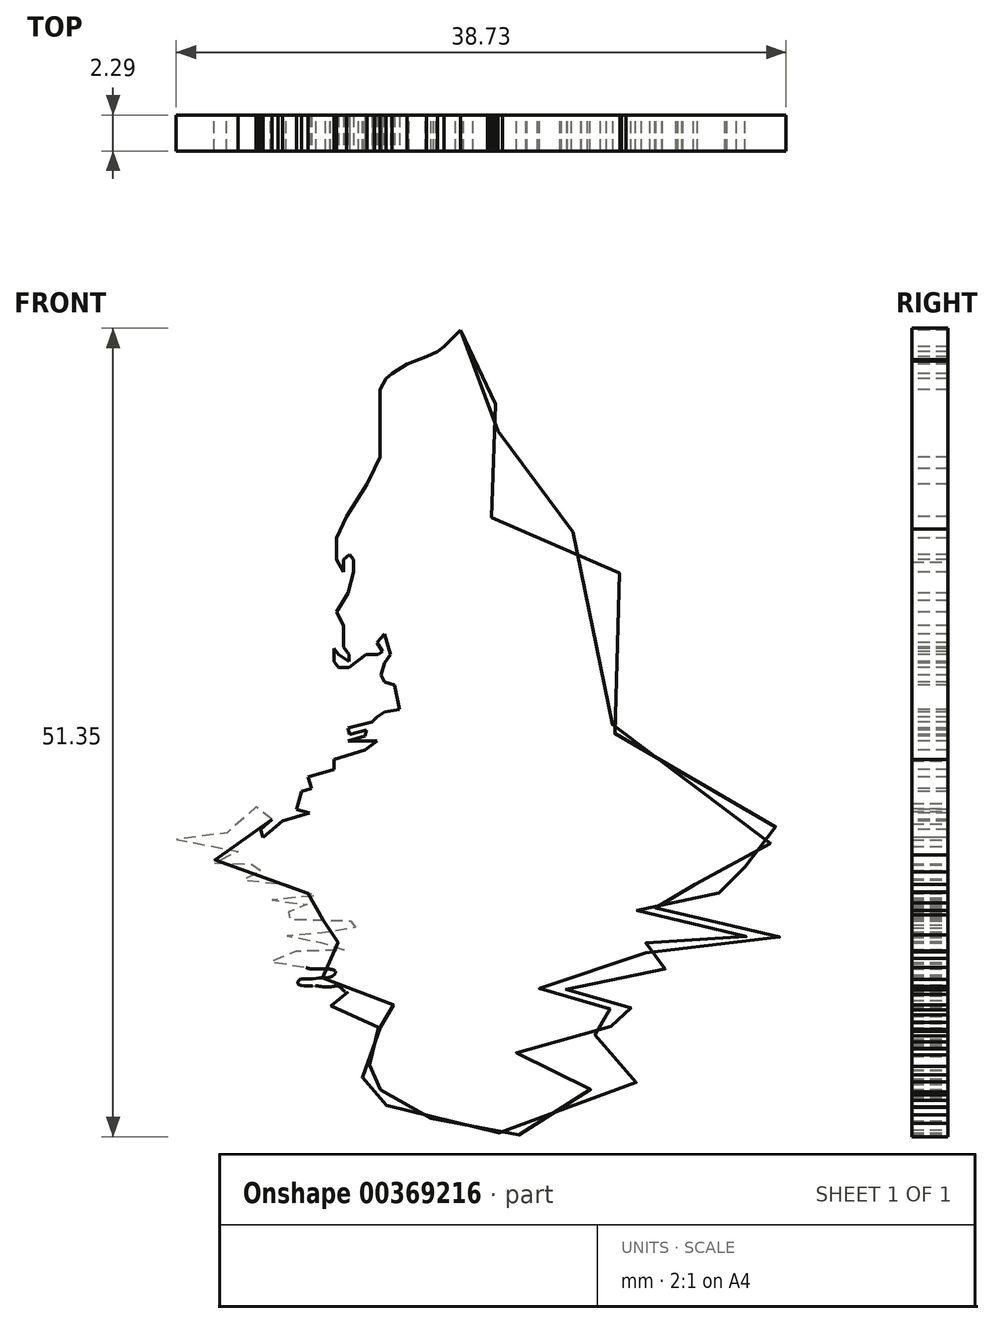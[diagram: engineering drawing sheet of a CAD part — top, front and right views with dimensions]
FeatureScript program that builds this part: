
annotation { "Feature Type Name" : "Feature", "Feature Type Description" : "" }
export const myFeature = defineFeature(function(context is Context, id is Id, definition is map)
    precondition{}
    {
        {
            var Q0;
            Q0=qCreatedBy(makeId("Front.planeOp"),FACE);
            var sketch = newSketch(context, id + "F0", { "sketchPlane" : qUnion([Q0])});
            skLineSegment(sketch, "E0", {"start": v(-10.1, 17.9) * mm, "end": v(-11.16, 16.85) * mm});
            skLineSegment(sketch, "E1", {"start": v(-11.16, 16.85) * mm, "end": v(-11.55, 16.52) * mm});
            skLineSegment(sketch, "E2", {"start": v(-11.55, 16.52) * mm, "end": v(-12.25, 16.22) * mm});
            skLineSegment(sketch, "E3", {"start": v(-12.25, 16.22) * mm, "end": v(-13.51, 15.72) * mm});
            skLineSegment(sketch, "E4", {"start": v(-13.51, 15.72) * mm, "end": v(-14.44, 15.12) * mm});
            skLineSegment(sketch, "E5", {"start": v(-14.44, 15.12) * mm, "end": v(-14.84, 14.82) * mm});
            skLineSegment(sketch, "E6", {"start": v(-14.84, 14.82) * mm, "end": v(-15.2, 14.13) * mm});
            skLineSegment(sketch, "E7", {"start": v(-15.2, 14.13) * mm, "end": v(-15.2, 12.83) * mm});
            skLineSegment(sketch, "E8", {"start": v(-15.2, 12.83) * mm, "end": v(-15.2, 11.57) * mm});
            skLineSegment(sketch, "E9", {"start": v(-15.2, 11.57) * mm, "end": v(-15.2, 10.54) * mm});
            skLineSegment(sketch, "E10", {"start": v(-15.2, 10.54) * mm, "end": v(-15.2, 9.81) * mm});
            skLineSegment(sketch, "E11", {"start": v(-15.2, 9.81) * mm, "end": v(-15.57, 9.08) * mm});
            skLineSegment(sketch, "E12", {"start": v(-15.57, 9.08) * mm, "end": v(-16.03, 8.12) * mm});
            skLineSegment(sketch, "E13", {"start": v(-16.03, 8.12) * mm, "end": v(-17.36, 6.04) * mm});
            skLineSegment(sketch, "E14", {"start": v(-17.36, 6.04) * mm, "end": v(-17.97, 4.7) * mm});
            skLineSegment(sketch, "E15", {"start": v(-17.97, 4.7) * mm, "end": v(-17.97, 3.31) * mm});
            skLineSegment(sketch, "E16", {"start": v(-17.97, 3.31) * mm, "end": v(-17.54, 2.52) * mm});
            skLineSegment(sketch, "E17", {"start": v(-17.54, 2.52) * mm, "end": v(-17.54, 3.31) * mm});
            skLineSegment(sketch, "E18", {"start": v(-17.54, 3.31) * mm, "end": v(-17.14, 3.63) * mm});
            skLineSegment(sketch, "E19", {"start": v(-17.14, 3.63) * mm, "end": v(-16.9, 3.31) * mm});
            skLineSegment(sketch, "E20", {"start": v(-16.9, 3.31) * mm, "end": v(-16.9, 2.52) * mm});
            skLineSegment(sketch, "E21", {"start": v(-16.9, 2.52) * mm, "end": v(-17.26, 1.18) * mm});
            skLineSegment(sketch, "E22", {"start": v(-17.26, 1.18) * mm, "end": v(-17.54, 0.7) * mm});
            skLineSegment(sketch, "E23", {"start": v(-17.54, 0.7) * mm, "end": v(-17.97, 0) * mm});
            skLineSegment(sketch, "E24", {"start": v(-17.97, 0) * mm, "end": v(-17.54, -0.87) * mm});
            skLineSegment(sketch, "E25", {"start": v(-17.54, -0.87) * mm, "end": v(-17.54, -1.42) * mm});
            skLineSegment(sketch, "E26", {"start": v(-17.54, -1.42) * mm, "end": v(-17.54, -2.25) * mm});
            skLineSegment(sketch, "E27", {"start": v(-17.54, -2.25) * mm, "end": v(-17.18, -2.73) * mm});
            skLineSegment(sketch, "E28", {"start": v(-17.18, -2.73) * mm, "end": v(-17.18, -3.16) * mm});
            skLineSegment(sketch, "E29", {"start": v(-17.18, -3.16) * mm, "end": v(-17.85, -2.73) * mm});
            skLineSegment(sketch, "E30", {"start": v(-17.85, -2.73) * mm, "end": v(-18.14, -2.34) * mm});
            skLineSegment(sketch, "E31", {"start": v(-18.14, -2.34) * mm, "end": v(-18.14, -3.16) * mm});
            skLineSegment(sketch, "E32", {"start": v(-18.14, -3.16) * mm, "end": v(-17.85, -3.54) * mm});
            skLineSegment(sketch, "E33", {"start": v(-17.85, -3.54) * mm, "end": v(-17.18, -3.54) * mm});
            skLineSegment(sketch, "E34", {"start": v(-17.18, -3.54) * mm, "end": v(-16.67, -3.16) * mm});
            skLineSegment(sketch, "E35", {"start": v(-16.67, -3.16) * mm, "end": v(-16.1, -2.73) * mm});
            skLineSegment(sketch, "E36", {"start": v(-16.1, -2.73) * mm, "end": v(-15.33, -2.73) * mm});
            skLineSegment(sketch, "E37", {"start": v(-15.33, -2.73) * mm, "end": v(-15.05, -2.51) * mm});
            skLineSegment(sketch, "E38", {"start": v(-15.05, -2.51) * mm, "end": v(-15.71, -2.51) * mm});
            skPoint(sketch, "E38.endSnap0", {"position": v(-15.71, -2.73) * mm});
            skLineSegment(sketch, "E39", {"start": v(-14.94, -1.42) * mm, "end": v(-15.4, -1.94) * mm});
            skLineSegment(sketch, "E40", {"start": v(-15.4, -1.94) * mm, "end": v(-15.05, -2.51) * mm});
            skLineSegment(sketch, "E41", {"start": v(-14.94, -1.42) * mm, "end": v(-14.54, -2.73) * mm});
            skLineSegment(sketch, "E42", {"start": v(-14.54, -2.73) * mm, "end": v(-14.94, -3.24) * mm});
            skLineSegment(sketch, "E43", {"start": v(-14.94, -3.24) * mm, "end": v(-15.15, -4) * mm});
            skLineSegment(sketch, "E44", {"start": v(-15.15, -4) * mm, "end": v(-14.94, -4.46) * mm});
            skLineSegment(sketch, "E45", {"start": v(-14.94, -4.46) * mm, "end": v(-14.29, -4.64) * mm});
            skLineSegment(sketch, "E46", {"start": v(-14.29, -4.64) * mm, "end": v(-13.99, -6.2) * mm});
            skLineSegment(sketch, "E47", {"start": v(-13.99, -6.2) * mm, "end": v(-14.94, -6.38) * mm});
            skLineSegment(sketch, "E48", {"start": v(-14.94, -6.38) * mm, "end": v(-15.4, -6.67) * mm});
            skLineSegment(sketch, "E49", {"start": v(-15.4, -6.67) * mm, "end": v(-15.71, -6.99) * mm});
            skLineSegment(sketch, "E50", {"start": v(-15.71, -6.99) * mm, "end": v(-17.26, -7.38) * mm});
            skLineSegment(sketch, "E51", {"start": v(-17.26, -7.38) * mm, "end": v(-17.16, -7.79) * mm});
            skLineSegment(sketch, "E52", {"start": v(-17.16, -7.79) * mm, "end": v(-16.07, -7.51) * mm});
            skLineSegment(sketch, "E53", {"start": v(-16.07, -7.51) * mm, "end": v(-16.17, -7.9) * mm});
            skLineSegment(sketch, "E54", {"start": v(-16.17, -7.9) * mm, "end": v(-17.26, -8.2) * mm});
            skLineSegment(sketch, "E55", {"start": v(-17.26, -8.2) * mm, "end": v(-15.4, -8.2) * mm});
            skLineSegment(sketch, "E56", {"start": v(-15.4, -8.2) * mm, "end": v(-16.17, -8.8) * mm});
            skLineSegment(sketch, "E57", {"start": v(-16.17, -8.8) * mm, "end": v(-17.26, -9.11) * mm});
            skLineSegment(sketch, "E58", {"start": v(-17.26, -9.11) * mm, "end": v(-18.14, -9.37) * mm});
            skLineSegment(sketch, "E59", {"start": v(-18.14, -9.37) * mm, "end": v(-18.14, -10.01) * mm});
            skLineSegment(sketch, "E60", {"start": v(-18.14, -10.01) * mm, "end": v(-19.06, -10.28) * mm});
            skLineSegment(sketch, "E61", {"start": v(-19.06, -10.28) * mm, "end": v(-19.77, -10.49) * mm});
            skLineSegment(sketch, "E62", {"start": v(-19.77, -10.49) * mm, "end": v(-19.56, -11.23) * mm});
            skLineSegment(sketch, "E63", {"start": v(-19.56, -11.23) * mm, "end": v(-20.2, -11.42) * mm});
            skLineSegment(sketch, "E64", {"start": v(-20.2, -11.42) * mm, "end": v(-20.51, -12.56) * mm});
            skLineSegment(sketch, "E65", {"start": v(-20.51, -12.56) * mm, "end": v(-19.68, -12.79) * mm});
            skLineSegment(sketch, "E66", {"start": v(-19.68, -12.79) * mm, "end": v(-21.41, -13.3) * mm});
            skLineSegment(sketch, "E67", {"start": v(-21.41, -13.3) * mm, "end": v(-22.65, -14.33) * mm});
            skLineSegment(sketch, "E68", {"start": v(-22.65, -14.33) * mm, "end": v(-22.8, -13.81) * mm});
            skPoint(sketch, "E68.endSnap0", {"position": v(-22.03, -13.81) * mm});
            skLineSegment(sketch, "E69", {"start": v(-22.8, -13.81) * mm, "end": v(-22.06, -13.2) * mm});
            skFitSpline(sketch, "E70", {"points": [v(-22.06, -13.2) * mm, v(-21.7, -12.85) * mm, v(-22.06, -12.4) * mm, v(-23.07, -12.24) * mm, v(-23.04, -12.66) * mm, v(-24.19, -12.52) * mm, v(-24.94, -14.1) * mm, v(-25.14, -14.47) * mm, v(-28.12, -14.33) * mm, v(-27.29, -14.83) * mm, v(-24.3, -15.03) * mm, v(-24.33, -15.4) * mm, v(-25.03, -15.47) * mm, v(-25.53, -15.59) * mm, v(-25.72, -15.8) * mm, v(-25.7, -16) * mm, v(-24.7, -16.06) * mm, v(-23.94, -16.09) * mm, v(-23.27, -16.03) * mm, v(-22.4, -16.12) * mm, v(-21.68, -16.48) * mm, v(-24.42, -16.5) * mm, v(-24.95, -16.93) * mm, v(-23.92, -17.03) * mm, v(-22.63, -17) * mm, v(-21.41, -17.06) * mm, v(-21.1, -17.42) * mm, v(-20.64, -17.79) * mm, v(-19.77, -17.89) * mm, v(-19.28, -17.99) * mm, v(-19.94, -18.19) * mm, v(-21.13, -18.32) * mm, v(-22.06, -18.32) * mm, v(-22.06, -18.59) * mm, v(-21, -18.62) * mm, v(-20.17, -18.62) * mm, v(-19.28, -18.55) * mm, v(-20.1, -18.85) * mm, v(-20.5, -19.08) * mm, v(-22.43, -19.08) * mm, v(-22.56, -19.38) * mm, v(-20.57, -19.51) * mm, v(-18.58, -19.58) * mm, v(-16.82, -19.61) * mm, v(-16.16, -19.58) * mm, v(-16.03, -19.81) * mm, v(-16.3, -20.05) * mm, v(-17.25, -19.98) * mm, v(-18.38, -20.01) * mm, v(-18.38, -20.38) * mm, v(-19.18, -20.38) * mm, v(-20.14, -20.34) * mm, v(-20.8, -20.34) * mm, v(-21.1, -20.54) * mm, v(-21.17, -20.84) * mm, v(-20.3, -20.94) * mm, v(-19.38, -20.97) * mm, v(-18.18, -21) * mm, v(-17.32, -21.04) * mm, v(-17.12, -21.3) * mm, v(-18.35, -21.57) * mm, v(-19.58, -21.54) * mm, v(-20.5, -21.57) * mm, v(-21.41, -21.57) * mm, v(-21.41, -21.94) * mm, v(-22.06, -21.97) * mm, v(-22.06, -22.4) * mm, v(-20.97, -22.47) * mm, v(-20.17, -22.4) * mm, v(-19.8, -22.63) * mm, v(-18.38, -22.7) * mm, v(-18.02, -22.9) * mm, v(-18.45, -23.23) * mm, v(-18.98, -23.26) * mm, v(-19.77, -23.33) * mm, v(-20.24, -23.33) * mm, v(-20.44, -23.6) * mm, v(-19.9, -23.76) * mm, v(-19.3, -23.76) * mm, v(-18.48, -23.83) * mm, v(-17.82, -23.8) * mm, v(-17.49, -24.1) * mm, v(-16.52, -24.13) * mm, v(-15, -24.16) * mm, v(-13.87, -24.2) * mm, v(-12.94, -24.36) * mm, v(-12.3, -24.62) * mm, v(-13.2, -24.92) * mm, v(-14.7, -24.96) * mm, v(-16.5, -25.02) * mm, v(-17.68, -25.02) * mm, v(-18.48, -25.05) * mm, v(-18.81, -25.22) * mm, v(-21.1, -25.22) * mm, v(-21.17, -25.39) * mm, v(-21, -25.52) * mm, v(-20.37, -25.59) * mm, v(-19.08, -25.69) * mm, v(-17.88, -25.69) * mm, v(-17.29, -25.69) * mm, v(-16.66, -25.98) * mm, v(-15.13, -26.05) * mm, v(-15.06, -26.25) * mm, v(-15.4, -26.42) * mm, v(-16, -26.48) * mm, v(-16.2, -26.81) * mm, v(-15.76, -26.95) * mm, v(-15.16, -27.08) * mm, v(-15.4, -27.48) * mm, v(-18.55, -27.54) * mm, v(-18.51, -28.17) * mm, v(-17.92, -28.1) * mm, v(-17.05, -28.24) * mm, v(-16.32, -28.2) * mm, v(-16.3, -28.7) * mm, v(-15.74, -28.81) * mm, v(-15.74, -29.12) * mm, v(-16.42, -29.1) * mm, v(-16.56, -29.33) * mm, v(-16.25, -29.54) * mm, v(-17.26, -29.63) * mm, v(-18.32, -29.68) * mm, v(-18.65, -29.73) * mm, v(-18.62, -30) * mm, v(-18.3, -29.96) * mm, v(-17.78, -29.96) * mm, v(-17.52, -30.27) * mm, v(-16.04, -30.34) * mm, v(-15.4, -30.34) * mm, v(-14.54, -30.38) * mm, v(-13.72, -30.38) * mm, v(-13.41, -30.57) * mm, v(-13.44, -30.83) * mm, v(-13.95, -30.83) * mm, v(-14.54, -30.92) * mm, v(-15.1, -30.95) * mm, v(-15.24, -31.13) * mm, v(-14.75, -31.37) * mm, v(-13.93, -31.4) * mm, v(-12.95, -31.49) * mm, v(-11.66, -31.84) * mm, v(-11.87, -32.05) * mm, v(-11.98, -32.24) * mm, v(-11.5, -32.33) * mm, v(-10.44, -32.45) * mm, v(-10.58, -32.75) * mm, v(-11.05, -32.9) * mm, v(-11.47, -32.92) * mm, v(-11.77, -32.94) * mm, v(-11.77, -33.17) * mm, v(-11.2, -33.17) * mm, v(-10.58, -33.15) * mm, v(-9.52, -33.15) * mm, v(-8.49, -33.15) * mm, v(-7.13, -33.13) * mm, v(-4.83, -33.2) * mm, v(-4.66, -32.54) * mm, v(-3.75, -32.44) * mm, v(-3.52, -31.93) * mm, v(-1.98, -31.9) * mm, v(-1.98, -31.46) * mm, v(-2.45, -31.46) * mm, v(-2.45, -31.06) * mm, v(-3.2, -31.02) * mm, v(-3.24, -30.67) * mm, v(-2.73, -30.67) * mm, v(-2.37, -30.4) * mm, v(1.26, -30.4) * mm, v(1.22, -29.96) * mm, v(-0.8, -29.84) * mm, v(-1.23, -29.45) * mm, v(-3.28, -29.6) * mm, v(-3.36, -28.97) * mm, v(-5.17, -28.82) * mm, v(-5.17, -28.22) * mm, v(-6.48, -28.1) * mm, v(-6.44, -27.75) * mm, v(-5.88, -27.75) * mm, v(-5.88, -27.28) * mm, v(-0.91, -27.24) * mm, v(-0.91, -26.96) * mm, v(-1.5, -26.92) * mm, v(-1.74, -26.65) * mm, v(-2.96, -26.6) * mm, v(-2.96, -26.21) * mm, v(-1.98, -26.25) * mm, v(-0.8, -26.33) * mm, v(0.39, -26.4) * mm, v(1.61, -26.53) * mm, v(1.93, -26.37) * mm, v(1.14, -26.1) * mm, v(0, -26.1) * mm, v(-1.19, -26.01) * mm, v(-1.98, -25.86) * mm, v(-2.02, -25.62) * mm, v(-1.19, -25.58) * mm, v(-0.48, -25.19) * mm, v(0.67, -25.26) * mm, v(0.74, -24.8) * mm, v(1.34, -24.71) * mm, v(2.72, -24.95) * mm, v(3.62, -24.8) * mm, v(3.62, -24.44) * mm, v(2.48, -24.36) * mm, v(1.3, -24.36) * mm, v(0.78, -24.08) * mm, v(-1.19, -24.04) * mm, v(-2.85, -24) * mm, v(-4.54, -24) * mm, v(-5.06, -24) * mm, v(-4.98, -23.73) * mm, v(-3.71, -23.73) * mm, v(-3.8, -23.13) * mm, v(-3.24, -23.13) * mm, v(-1.15, -23.21) * mm, v(1.1, -23.25) * mm, v(3.62, -23.17) * mm, v(2.68, -22.54) * mm, v(3.86, -22.54) * mm, v(3.82, -22.07) * mm, v(3.15, -22.19) * mm, v(2.2, -22.15) * mm, v(2.09, -21.83) * mm, v(0, -21.6) * mm, v(-0.76, -21.52) * mm, v(-1.23, -21.28) * mm, v(0, -21.04) * mm, v(1.5, -21) * mm, v(2.6, -21.32) * mm, v(3.7, -21.52) * mm, v(5.24, -21.6) * mm, v(7.14, -21.52) * mm, v(9.03, -21.48) * mm, v(10.53, -21.4) * mm, v(10.13, -20.65) * mm, v(9.27, -20.57) * mm, v(7.77, -20.65) * mm, v(6.19, -20.77) * mm, v(4.69, -20.89) * mm, v(3.78, -21) * mm, v(3.35, -20.6) * mm, v(2.28, -20.65) * mm, v(2.32, -20.21) * mm, v(2.24, -19.78) * mm, v(2.56, -19.54) * mm, v(2.72, -19.27) * mm, v(1.3, -19.39) * mm, v(1.02, -19.1) * mm, v(1.45, -18.83) * mm, v(2.76, -18.83) * mm, v(3.86, -18.95) * mm, v(4.61, -18.87) * mm, v(4.61, -18.52) * mm, v(3.94, -18.6) * mm, v(3.58, -18.28) * mm, v(4.26, -18.2) * mm, v(5.44, -18.32) * mm, v(6.58, -18.44) * mm, v(6.82, -18.08) * mm, v(6.39, -17.85) * mm, v(5.68, -17.89) * mm, v(4.85, -17.8) * mm, v(4.52, -17.86) * mm, v(4.1, -17.74) * mm, v(4.08, -17.4) * mm, v(4.78, -17.32) * mm, v(5.95, -17.28) * mm, v(7.03, -17.25) * mm, v(7.4, -16.92) * mm, v(6.75, -16.83) * mm, v(6.82, -16.52) * mm, v(7.57, -16.52) * mm, v(7.95, -16.17) * mm, v(7.62, -15.94) * mm, v(6.99, -15.82) * mm, v(6.56, -15.7) * mm, v(6.46, -15.37) * mm, v(4.96, -13.59) * mm, v(7.63, -13.97) * mm, v(9.27, -14.48) * mm, v(10.54, -15.44) * mm, v(10.14, -14.15) * mm, v(9.44, -12.75) * mm, v(8.57, -11.55) * mm, v(6.71, -10.47) * mm, v(4.67, -9.93) * mm, v(2.84, -9.37) * mm, v(2.03, -9.47) * mm, v(0.88, -8.83) * mm, v(0, -8.2) * mm, v(-0.43, -7.35) * mm, v(-0.62, -6.23) * mm, v(-0.8, -5.14) * mm, v(0.24, -4.06) * mm, v(0.35, -2.72) * mm, v(0, -2.05) * mm, v(-0.43, -1.69) * mm, v(0, -1.38) * mm, v(0, 0) * mm, v(0, 2.34) * mm, v(-0.44, 3.87) * mm, v(-1.27, 5.13) * mm, v(-2.8, 5.1) * mm, v(-4.38, 4.53) * mm, v(-5.71, 3.74) * mm, v(-6.57, 3.17) * mm, v(-6.84, 3.54) * mm, v(-7.54, 4.96) * mm, v(-8.3, 6.32) * mm, v(-9.06, 7.72) * mm, v(-9.92, 9.14) * mm, v(-9.76, 9.54) * mm, v(-9.5, 10.48) * mm, v(-8.78, 11.27) * mm, v(-8.34, 11.35) * mm, v(-7.55, 11.6) * mm, v(-7.5, 12.16) * mm, v(-7.75, 12.4) * mm, v(-7.75, 12.81) * mm, v(-7.97, 13.02) * mm, v(-7.88, 13.24) * mm, v(-8.2, 13.5) * mm, v(-8.1, 13.86) * mm, v(-8.57, 14.01) * mm, v(-8.88, 14.08) * mm, v(-9.13, 14.53) * mm, v(-9.28, 15.24) * mm, v(-8.93, 15.72) * mm, v(-8.8, 16.02) * mm, v(-8.53, 15.91) * mm, v(-8.39, 16.36) * mm, v(-8.54, 17.14) * mm, v(-8.8, 17.59) * mm, v(-9.2, 17.98) * mm, v(-10.1, 17.9) * mm], "startDerivative": vector(213.03, 138.53) * mm, "endDerivative": vector(-325.18, -77.64) * mm});
            skSolve(sketch);
        }
        {
            var Q0;
            Q0=makeQuery(id+"F0.imprint","IMPRINT",FACE,{"disambiguationData":[TD([[makeQuery(id+"F0.imprint","IMPRINT",EDGE,{"derivedFrom":sQuery(id+"F0.wireOp",EDGE,"E0")}),1.0]])]});
            extrude(context, id + "F1", {"entities" : qUnion([Q0]), "oppositeDirection" : true, "depth" : 2.3 * mm});
        }
    });
